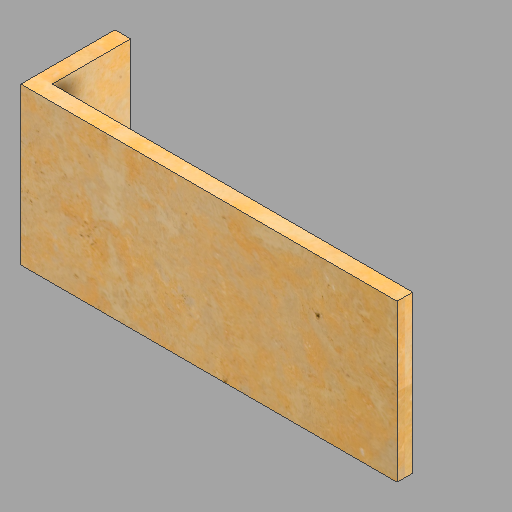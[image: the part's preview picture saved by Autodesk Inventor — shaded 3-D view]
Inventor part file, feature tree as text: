
AUTODESK INVENTOR PART (.ipt)
format: ipt  version: 2023 (Build 270158030, 158C)  size: 292,352 bytes
history: native  units: in
note: dims shown in document units (in); Inventor stores cm internally (conversion verified against a paired STEP export)
features: extrude x2, sketch x2
ambient origin geometry x8: Origin, YZ Plane, XZ Plane, XY Plane, X Axis, Y Axis, Z Axis, Center Point
bodies: Solid1 (feature_tree)
feature tree (4):
  extrude  "Extrusion1"  Depth=1.0in
  extrude  "Extrusion2"  Depth=1.0in
  sketch  "Sketch1"  dims[d0=10.0in d1=1.0in]
  sketch  "Sketch2"  dims[d2=24.0in d3=0.0in d4=1.0in d5=5.0in d6=0.0in]
